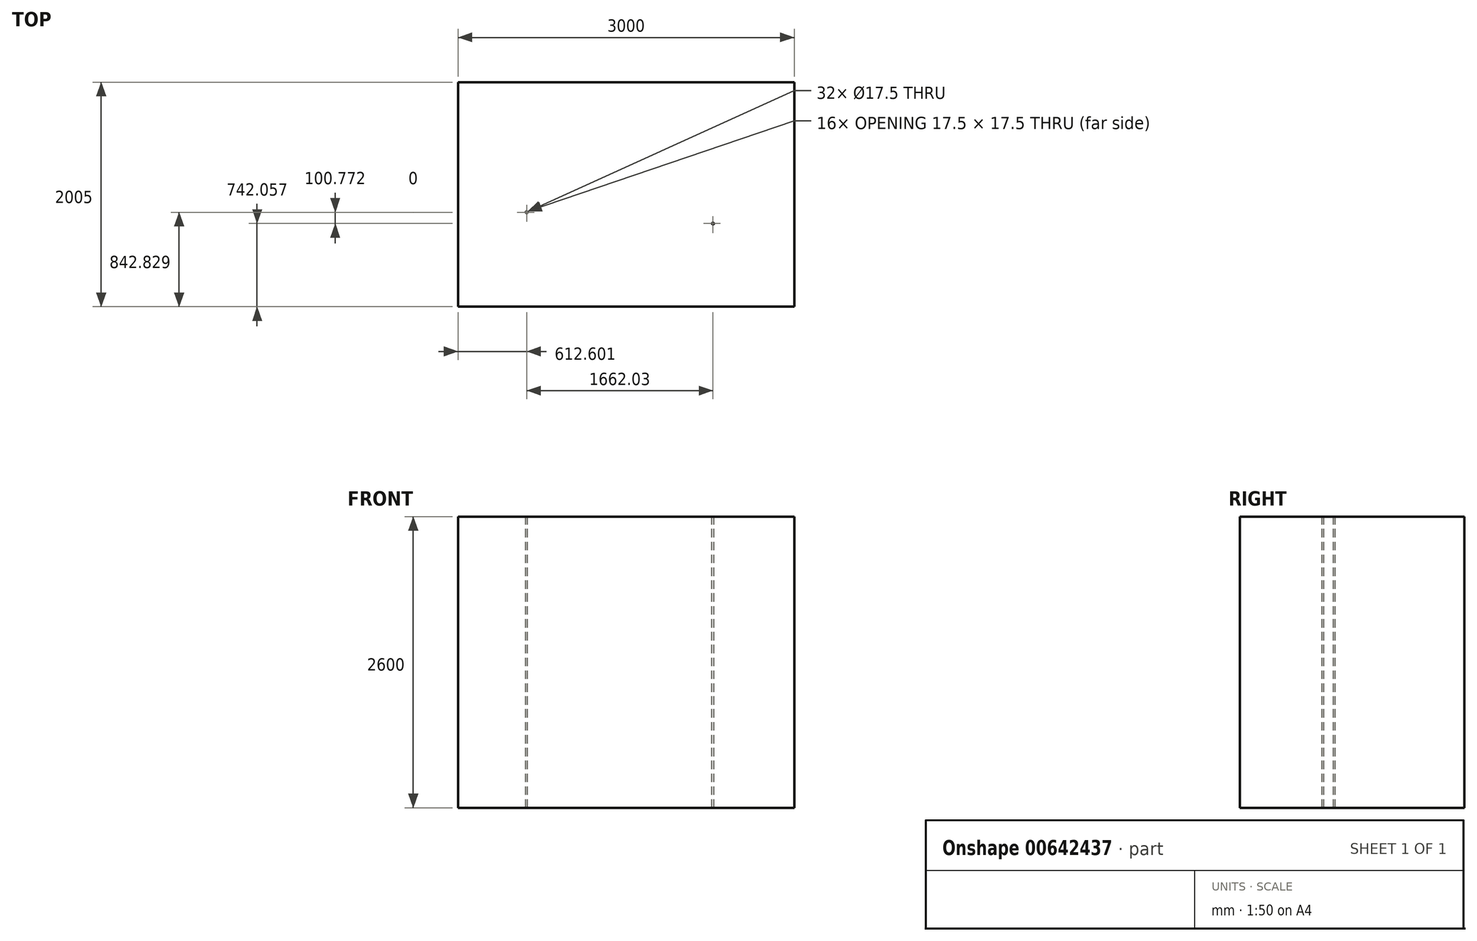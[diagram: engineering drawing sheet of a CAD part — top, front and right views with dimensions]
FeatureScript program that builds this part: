
annotation { "Feature Type Name" : "Feature", "Feature Type Description" : "" }
export const myFeature = defineFeature(function(context is Context, id is Id, definition is map)
    precondition{}
    {
        {
            var Q0;
            Q0=qCreatedBy(makeId("Front.planeOp"),FACE);
            var sketch = newSketch(context, id + "F0", { "sketchPlane" : qUnion([Q0])});
            skLineSegment(sketch, "E0.bottom", {"start": v(0, 0) * mm, "end": v(-3000, 0) * mm});
            skLineSegment(sketch, "E0.top", {"start": v(0, 2600) * mm, "end": v(-3000, 2600) * mm});
            skLineSegment(sketch, "E0.left", {"start": v(0, 0) * mm, "end": v(0, 2600) * mm});
            skLineSegment(sketch, "E0.right", {"start": v(-3000, 0) * mm, "end": v(-3000, 2600) * mm});
            skSolve(sketch);
        }
        {
            var Q0;
            Q0 = qSketchRegion(id + "F0", true);
            extrude(context, id + "F1", {"entities" : qUnion([Q0]), "depth" : 2005 * mm, "offsetDistance" : 25 * mm});
        }
        {
            var Q0;
            Q0=makeQuery(id+"F1.opExtrude","SWEPT_FACE",FACE,{"disambiguationData":[OSD([sQuery(id+"F0.wireOp",EDGE,"E0.top")])]});
            var sketch = newSketch(context, id + "F2", { "sketchPlane" : qUnion([Q0])});
            skLineSegment(sketch, "E1", {"start": v(-2387.4, -1162.17) * mm, "end": v(-725.37, -1262.94) * mm});
            skSolve(sketch);
        }
        {
            var Q0;
            Q0=sQuery(id+"F2.wireOp",VERTEX,"E1.start");
            var Q1;
            Q1=sQuery(id+"F2.wireOp",VERTEX,"E1.end");
            var Q2;
            Q2=makeQuery(id+"F1.opExtrude","SWEPT_BODY",BODY,{"disambiguationData":[OSD([sQuery(id+"F0.wireOp",EDGE,"E0.bottom"),sQuery(id+"F0.wireOp",EDGE,"E0.top"),sQuery(id+"F0.wireOp",EDGE,"E0.left"),sQuery(id+"F0.wireOp",EDGE,"E0.right")])]});
            hole(context, id + "F3", {"style" : HoleStyle.SIMPLE, "endStyle" : HoleEndStyle.BLIND, "standardTappedOrClearance" : lookupTablePath({ "standard" : "ISO", "fit" : "Normal", "size" : "M16", "type" : "Clearance" }), "standardBlindInLast" : lookupTablePath({ "fit" : "Standard", "standard" : "ISO", "size" : "M16", "type" : "Clearance" }), "holeDiameter" : 17.5 * mm, "majorDiameter" : 5 * mm, "holeDepth" : 3000 * mm, "isTappedThrough" : true, "tappedDepth" : 12 * mm, "tapClearance" : 3, "startFromSketch" : true, "locations" : qUnion([Q0, Q1]), "scope" : qUnion([Q2])});
        }
    });
